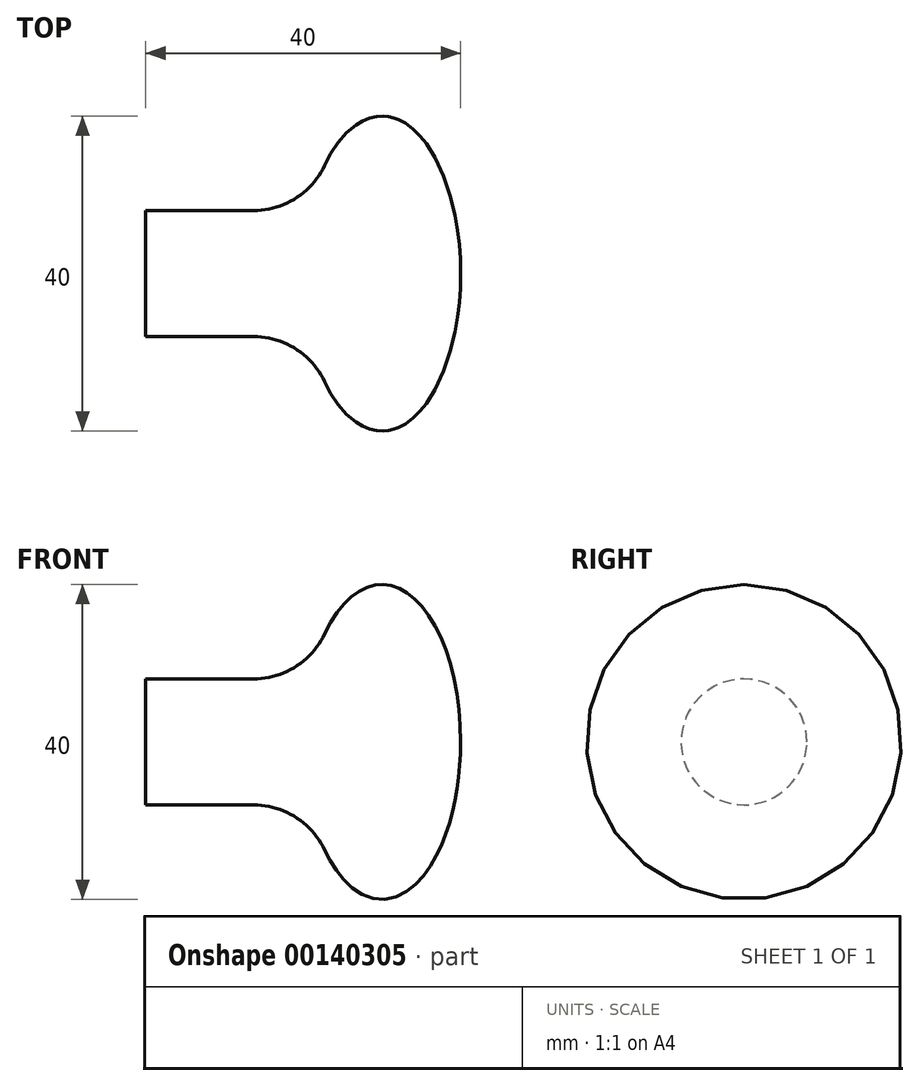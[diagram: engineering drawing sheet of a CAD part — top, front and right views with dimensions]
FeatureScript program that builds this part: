
annotation { "Feature Type Name" : "Feature", "Feature Type Description" : "" }
export const myFeature = defineFeature(function(context is Context, id is Id, definition is map)
    precondition{}
    {
        {
            var Q0;
            Q0=qCreatedBy(makeId("Front.planeOp"),FACE);
            var sketch = newSketch(context, id + "F0", { "sketchPlane" : qUnion([Q0])});
            skLineSegment(sketch, "E0.top", {"start": v(0, 8) * mm, "end": v(20.83, 8) * mm});
            skLineSegment(sketch, "E0.left", {"start": v(0, 0) * mm, "end": v(0, 8) * mm});
            skEllipticalArc(sketch, "E1", {});
            skLineSegment(sketch, "E2", {"start": v(0, 0) * mm, "end": v(40, 0) * mm});
            const initialGuessF0  = {"E1": [0.03, 0, 0, 1, 0.02, 0.01, 4.71238898038469, 1.1592794807274085]};
            skSetInitialGuess(sketch, initialGuessF0);
            skSolve(sketch);
        }
        {
            var Q0;
            Q0=makeQuery(id+"F0.imprint","IMPRINT",FACE,{"disambiguationData":[TD([[makeQuery(id+"F0.imprint","IMPRINT",EDGE,{"derivedFrom":sQuery(id+"F0.wireOp",EDGE,"E0.top")}),-1.0]])]});
            var Q1;
            Q1=sQuery(id+"F0.wireOp",EDGE,"E2");
            revolve(context, id + "F1", {"entities" : qUnion([Q0]), "axis" : qUnion([Q1]), "revolveType" : RevolveType.FULL});
        }
        {
            var Q0;
            Q0=makeQuery(id+"F1.opRevolve","SWEPT_EDGE",EDGE,{"disambiguationData":[OSD([sQuery(id+"F0.wireOp",EDGE,"E0.top"),sQuery(id+"F0.wireOp",EDGE,"E1")])]});
            fillet(context, id + "F2", {"entities" : qUnion([Q0]), "radius" : 10 * mm, "tangentPropagation" : true, "allowEdgeOverflow" : false});
        }
    });
